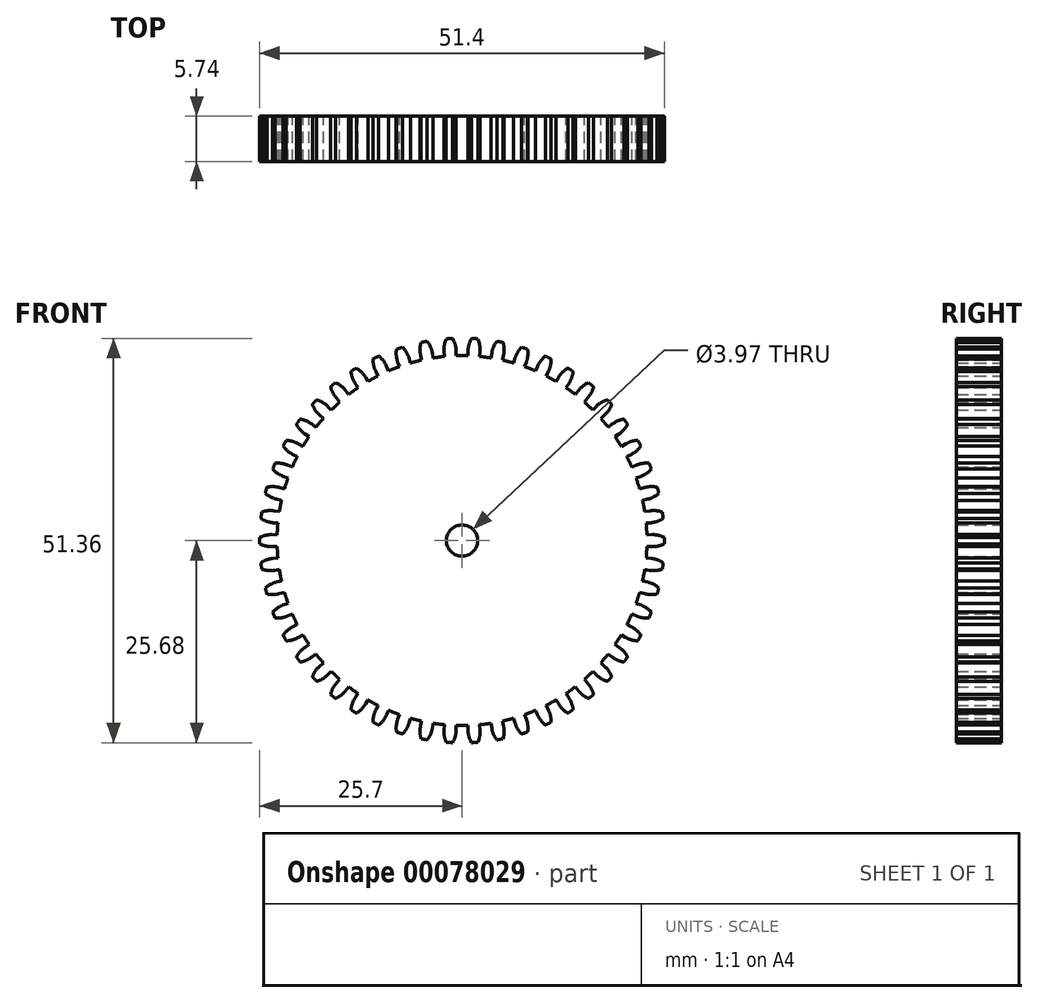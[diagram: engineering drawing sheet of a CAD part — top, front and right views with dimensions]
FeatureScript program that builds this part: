
annotation { "Feature Type Name" : "Feature", "Feature Type Description" : "" }
export const myFeature = defineFeature(function(context is Context, id is Id, definition is map)
    precondition{}
    {
        {
            var Q0;
            Q0=qCreatedBy(makeId("Front.planeOp"),FACE);
            var sketch = newSketch(context, id + "F0", { "sketchPlane" : qUnion([Q0])});
            skCircle(sketch, "E0", {"center": v(0, 0) * mm, "radius": 25.7 * mm, "construction": true});
            skCircle(sketch, "E1", {"center": v(0, 0) * mm, "radius": 24.13 * mm, "construction": true});
            skCircle(sketch, "E2", {"center": v(0, 0) * mm, "radius": 23.5 * mm, "construction": true});
            skLineSegment(sketch, "E3", {"start": v(0, 0) * mm, "end": v(23.45, 1.48) * mm, "construction": true});
            skLineSegment(sketch, "E4", {"start": v(0, 0) * mm, "end": v(6.61, 0) * mm, "construction": true});
            skLineSegment(sketch, "E5", {"start": v(0, 0) * mm, "end": v(6.9, 0.22) * mm, "construction": true});
            skLineSegment(sketch, "E6", {"start": v(0, 0) * mm, "end": v(7.15, 0.11) * mm, "construction": true});
            skArc(sketch, "E7", {"start": v(25.7, 0.4) * mm, "mid": v(25.7, 0.2) * mm, "end": v(25.7, 0) * mm});
            skArc(sketch, "E8", {"start": v(23.45, 1.48) * mm, "mid": v(23.47, 1.1) * mm, "end": v(23.48, 0.74) * mm});
            skLineSegment(sketch, "E9", {"start": v(23.48, 0.74) * mm, "end": v(24.12, 0.76) * mm});
            skArc(sketch, "E10", {"start": v(24.12, 0.76) * mm, "mid": v(24.93, 0.68) * mm, "end": v(25.7, 0.4) * mm});
            skLineSegment(sketch, "E11", {"start": v(0, 0) * mm, "end": v(23.45, 1.48) * mm});
            skLineSegment(sketch, "E12", {"start": v(0, 0) * mm, "end": v(25.7, 0) * mm});
            skArc(sketch, "E13.MirrorCS", {"start": v(23.45, -1.48) * mm, "mid": v(23.47, -1.1) * mm, "end": v(23.48, -0.74) * mm});
            skLineSegment(sketch, "E14.MirrorCS", {"start": v(23.48, -0.74) * mm, "end": v(24.12, -0.76) * mm});
            skArc(sketch, "E15.MirrorCS", {"start": v(24.12, -0.76) * mm, "mid": v(24.93, -0.68) * mm, "end": v(25.7, -0.4) * mm});
            skArc(sketch, "E16.MirrorCS", {"start": v(25.7, -0.4) * mm, "mid": v(25.7, -0.2) * mm, "end": v(25.7, 0) * mm});
            skArc(sketch, "E17.1.0", {"start": v(23.08, 4.4) * mm, "mid": v(23.15, 4.04) * mm, "end": v(23.2, 3.68) * mm});
            skLineSegment(sketch, "E17.1.1", {"start": v(23.2, 3.68) * mm, "end": v(23.83, 3.77) * mm});
            skArc(sketch, "E17.1.2", {"start": v(23.83, 3.77) * mm, "mid": v(24.65, 3.8) * mm, "end": v(25.45, 3.62) * mm});
            skArc(sketch, "E17.1.3", {"start": v(25.45, 3.62) * mm, "mid": v(25.48, 3.42) * mm, "end": v(25.5, 3.22) * mm});
            skArc(sketch, "E17.1.4", {"start": v(25.55, 2.82) * mm, "mid": v(25.53, 3.02) * mm, "end": v(25.5, 3.22) * mm});
            skArc(sketch, "E17.1.5", {"start": v(24.02, 2.27) * mm, "mid": v(24.82, 2.45) * mm, "end": v(25.55, 2.82) * mm});
            skLineSegment(sketch, "E17.1.6", {"start": v(23.4, 2.21) * mm, "end": v(24.02, 2.27) * mm});
            skArc(sketch, "E17.1.7", {"start": v(23.45, 1.48) * mm, "mid": v(23.42, 1.84) * mm, "end": v(23.4, 2.21) * mm});
            skArc(sketch, "E17.2.0", {"start": v(22.35, 7.26) * mm, "mid": v(22.46, 6.9) * mm, "end": v(22.56, 6.55) * mm});
            skLineSegment(sketch, "E17.2.1", {"start": v(22.56, 6.55) * mm, "end": v(23.17, 6.73) * mm});
            skArc(sketch, "E17.2.2", {"start": v(23.17, 6.73) * mm, "mid": v(23.98, 6.86) * mm, "end": v(24.8, 6.78) * mm});
            skArc(sketch, "E17.2.3", {"start": v(24.8, 6.78) * mm, "mid": v(24.85, 6.59) * mm, "end": v(24.9, 6.4) * mm});
            skArc(sketch, "E17.2.4", {"start": v(25, 6) * mm, "mid": v(24.95, 6.2) * mm, "end": v(24.9, 6.4) * mm});
            skArc(sketch, "E17.2.5", {"start": v(23.55, 5.26) * mm, "mid": v(24.32, 5.54) * mm, "end": v(25, 6) * mm});
            skLineSegment(sketch, "E17.2.6", {"start": v(22.93, 5.13) * mm, "end": v(23.55, 5.26) * mm});
            skArc(sketch, "E17.2.7", {"start": v(23.08, 4.4) * mm, "mid": v(23, 4.76) * mm, "end": v(22.93, 5.13) * mm});
            skArc(sketch, "E17.3.0", {"start": v(21.26, 10) * mm, "mid": v(21.41, 9.67) * mm, "end": v(21.56, 9.33) * mm});
            skLineSegment(sketch, "E17.3.1", {"start": v(21.56, 9.33) * mm, "end": v(22.15, 9.58) * mm});
            skArc(sketch, "E17.3.2", {"start": v(22.15, 9.58) * mm, "mid": v(22.93, 9.81) * mm, "end": v(23.75, 9.84) * mm});
            skArc(sketch, "E17.3.3", {"start": v(23.75, 9.84) * mm, "mid": v(23.82, 9.65) * mm, "end": v(23.9, 9.46) * mm});
            skArc(sketch, "E17.3.4", {"start": v(24.05, 9.09) * mm, "mid": v(23.97, 9.27) * mm, "end": v(23.9, 9.46) * mm});
            skArc(sketch, "E17.3.5", {"start": v(22.7, 8.17) * mm, "mid": v(23.43, 8.55) * mm, "end": v(24.05, 9.09) * mm});
            skLineSegment(sketch, "E17.3.6", {"start": v(22.1, 7.96) * mm, "end": v(22.7, 8.17) * mm});
            skArc(sketch, "E17.3.7", {"start": v(22.35, 7.26) * mm, "mid": v(22.23, 7.61) * mm, "end": v(22.1, 7.96) * mm});
            skArc(sketch, "E17.4.0", {"start": v(19.84, 12.59) * mm, "mid": v(20.03, 12.28) * mm, "end": v(20.22, 11.96) * mm});
            skLineSegment(sketch, "E17.4.1", {"start": v(20.22, 11.96) * mm, "end": v(20.77, 12.28) * mm});
            skArc(sketch, "E17.4.2", {"start": v(20.77, 12.28) * mm, "mid": v(21.52, 12.6) * mm, "end": v(22.33, 12.74) * mm});
            skArc(sketch, "E17.4.3", {"start": v(22.33, 12.74) * mm, "mid": v(22.43, 12.56) * mm, "end": v(22.53, 12.38) * mm});
            skArc(sketch, "E17.4.4", {"start": v(22.72, 12.03) * mm, "mid": v(22.62, 12.2) * mm, "end": v(22.53, 12.38) * mm});
            skArc(sketch, "E17.4.5", {"start": v(21.5, 10.95) * mm, "mid": v(22.18, 11.41) * mm, "end": v(22.72, 12.03) * mm});
            skLineSegment(sketch, "E17.4.6", {"start": v(20.93, 10.67) * mm, "end": v(21.5, 10.95) * mm});
            skArc(sketch, "E17.4.7", {"start": v(21.26, 10) * mm, "mid": v(21.1, 10.34) * mm, "end": v(20.93, 10.67) * mm});
            skArc(sketch, "E17.5.0", {"start": v(18.1, 14.98) * mm, "mid": v(18.34, 14.7) * mm, "end": v(18.56, 14.4) * mm});
            skLineSegment(sketch, "E17.5.1", {"start": v(18.56, 14.4) * mm, "end": v(19.07, 14.79) * mm});
            skArc(sketch, "E17.5.2", {"start": v(19.07, 14.79) * mm, "mid": v(19.77, 15.2) * mm, "end": v(20.56, 15.43) * mm});
            skArc(sketch, "E17.5.3", {"start": v(20.56, 15.43) * mm, "mid": v(20.68, 15.27) * mm, "end": v(20.8, 15.1) * mm});
            skArc(sketch, "E17.5.4", {"start": v(21.03, 14.78) * mm, "mid": v(20.91, 14.95) * mm, "end": v(20.8, 15.1) * mm});
            skArc(sketch, "E17.5.5", {"start": v(19.96, 13.56) * mm, "mid": v(20.57, 14.1) * mm, "end": v(21.03, 14.78) * mm});
            skLineSegment(sketch, "E17.5.6", {"start": v(19.43, 13.2) * mm, "end": v(19.96, 13.56) * mm});
            skArc(sketch, "E17.5.7", {"start": v(19.84, 12.59) * mm, "mid": v(19.64, 12.9) * mm, "end": v(19.43, 13.2) * mm});
            skArc(sketch, "E17.6.0", {"start": v(16.08, 17.13) * mm, "mid": v(16.35, 16.87) * mm, "end": v(16.61, 16.61) * mm});
            skLineSegment(sketch, "E17.6.1", {"start": v(16.61, 16.61) * mm, "end": v(17.06, 17.06) * mm});
            skArc(sketch, "E17.6.2", {"start": v(17.06, 17.06) * mm, "mid": v(17.7, 17.56) * mm, "end": v(18.46, 17.89) * mm});
            skArc(sketch, "E17.6.3", {"start": v(18.46, 17.89) * mm, "mid": v(18.6, 17.74) * mm, "end": v(18.74, 17.6) * mm});
            skArc(sketch, "E17.6.4", {"start": v(19.01, 17.3) * mm, "mid": v(18.88, 17.45) * mm, "end": v(18.74, 17.6) * mm});
            skArc(sketch, "E17.6.5", {"start": v(18.1, 15.96) * mm, "mid": v(18.64, 16.57) * mm, "end": v(19.01, 17.3) * mm});
            skLineSegment(sketch, "E17.6.6", {"start": v(17.62, 15.54) * mm, "end": v(18.1, 15.96) * mm});
            skArc(sketch, "E17.6.7", {"start": v(18.1, 14.98) * mm, "mid": v(17.87, 15.26) * mm, "end": v(17.62, 15.54) * mm});
            skArc(sketch, "E17.7.0", {"start": v(13.81, 19) * mm, "mid": v(14.1, 18.79) * mm, "end": v(14.4, 18.56) * mm});
            skLineSegment(sketch, "E17.7.1", {"start": v(14.4, 18.56) * mm, "end": v(14.79, 19.07) * mm});
            skArc(sketch, "E17.7.2", {"start": v(14.79, 19.07) * mm, "mid": v(15.37, 19.64) * mm, "end": v(16.07, 20.06) * mm});
            skArc(sketch, "E17.7.3", {"start": v(16.07, 20.06) * mm, "mid": v(16.23, 19.93) * mm, "end": v(16.38, 19.8) * mm});
            skArc(sketch, "E17.7.4", {"start": v(16.7, 19.55) * mm, "mid": v(16.54, 19.68) * mm, "end": v(16.38, 19.8) * mm});
            skArc(sketch, "E17.7.5", {"start": v(15.96, 18.1) * mm, "mid": v(16.42, 18.78) * mm, "end": v(16.7, 19.55) * mm});
            skLineSegment(sketch, "E17.7.6", {"start": v(15.54, 17.62) * mm, "end": v(15.96, 18.1) * mm});
            skArc(sketch, "E17.7.7", {"start": v(16.08, 17.13) * mm, "mid": v(15.81, 17.38) * mm, "end": v(15.54, 17.62) * mm});
            skArc(sketch, "E17.8.0", {"start": v(11.32, 20.59) * mm, "mid": v(11.64, 20.4) * mm, "end": v(11.96, 20.22) * mm});
            skLineSegment(sketch, "E17.8.1", {"start": v(11.96, 20.22) * mm, "end": v(12.28, 20.77) * mm});
            skArc(sketch, "E17.8.2", {"start": v(12.28, 20.77) * mm, "mid": v(12.78, 21.42) * mm, "end": v(13.43, 21.92) * mm});
            skArc(sketch, "E17.8.3", {"start": v(13.43, 21.92) * mm, "mid": v(13.6, 21.81) * mm, "end": v(13.77, 21.7) * mm});
            skArc(sketch, "E17.8.4", {"start": v(14.11, 21.48) * mm, "mid": v(13.94, 21.6) * mm, "end": v(13.77, 21.7) * mm});
            skArc(sketch, "E17.8.5", {"start": v(13.56, 19.96) * mm, "mid": v(13.93, 20.69) * mm, "end": v(14.11, 21.48) * mm});
            skLineSegment(sketch, "E17.8.6", {"start": v(13.2, 19.43) * mm, "end": v(13.56, 19.96) * mm});
            skArc(sketch, "E17.8.7", {"start": v(13.81, 19) * mm, "mid": v(13.5, 19.22) * mm, "end": v(13.2, 19.43) * mm});
            skArc(sketch, "E17.9.0", {"start": v(8.65, 21.85) * mm, "mid": v(9, 21.7) * mm, "end": v(9.33, 21.56) * mm});
            skLineSegment(sketch, "E17.9.1", {"start": v(9.33, 21.56) * mm, "end": v(9.58, 22.15) * mm});
            skArc(sketch, "E17.9.2", {"start": v(9.58, 22.15) * mm, "mid": v(10, 22.85) * mm, "end": v(10.58, 23.43) * mm});
            skArc(sketch, "E17.9.3", {"start": v(10.58, 23.43) * mm, "mid": v(10.76, 23.34) * mm, "end": v(10.94, 23.26) * mm});
            skArc(sketch, "E17.9.4", {"start": v(11.3, 23.08) * mm, "mid": v(11.13, 23.17) * mm, "end": v(10.94, 23.26) * mm});
            skArc(sketch, "E17.9.5", {"start": v(10.95, 21.5) * mm, "mid": v(11.23, 22.27) * mm, "end": v(11.3, 23.08) * mm});
            skLineSegment(sketch, "E17.9.6", {"start": v(10.67, 20.93) * mm, "end": v(10.95, 21.5) * mm});
            skArc(sketch, "E17.9.7", {"start": v(11.32, 20.59) * mm, "mid": v(11, 20.76) * mm, "end": v(10.67, 20.93) * mm});
            skCircle(sketch, "E18", {"center": v(0, 0) * mm, "radius": 1.98 * mm});
            skArc(sketch, "E19.1.10.0", {"start": v(5.84, 22.76) * mm, "mid": v(6.2, 22.66) * mm, "end": v(6.55, 22.56) * mm});
            skLineSegment(sketch, "E19.4.10.0", {"start": v(6.55, 22.56) * mm, "end": v(6.73, 23.17) * mm});
            skArc(sketch, "E19.7.10.0", {"start": v(6.73, 23.17) * mm, "mid": v(7.06, 23.92) * mm, "end": v(7.56, 24.57) * mm});
            skArc(sketch, "E19.11.10.0", {"start": v(7.56, 24.57) * mm, "mid": v(7.75, 24.5) * mm, "end": v(7.94, 24.45) * mm});
            skArc(sketch, "E19.15.10.0", {"start": v(8.33, 24.32) * mm, "mid": v(8.13, 24.38) * mm, "end": v(7.94, 24.45) * mm});
            skArc(sketch, "E19.19.10.0", {"start": v(8.17, 22.7) * mm, "mid": v(8.35, 23.5) * mm, "end": v(8.33, 24.32) * mm});
            skLineSegment(sketch, "E19.23.10.0", {"start": v(7.96, 22.1) * mm, "end": v(8.17, 22.7) * mm});
            skArc(sketch, "E19.26.10.0", {"start": v(8.65, 21.85) * mm, "mid": v(8.3, 21.98) * mm, "end": v(7.96, 22.1) * mm});
            skArc(sketch, "E19.1.11.0", {"start": v(2.94, 23.3) * mm, "mid": v(3.31, 23.26) * mm, "end": v(3.68, 23.2) * mm});
            skLineSegment(sketch, "E19.4.11.0", {"start": v(3.68, 23.2) * mm, "end": v(3.77, 23.83) * mm});
            skArc(sketch, "E19.7.11.0", {"start": v(3.77, 23.83) * mm, "mid": v(4, 24.62) * mm, "end": v(4.42, 25.32) * mm});
            skArc(sketch, "E19.11.11.0", {"start": v(4.42, 25.32) * mm, "mid": v(4.62, 25.29) * mm, "end": v(4.82, 25.25) * mm});
            skArc(sketch, "E19.15.11.0", {"start": v(5.21, 25.17) * mm, "mid": v(5.01, 25.21) * mm, "end": v(4.82, 25.25) * mm});
            skArc(sketch, "E19.19.11.0", {"start": v(5.26, 23.55) * mm, "mid": v(5.34, 24.36) * mm, "end": v(5.21, 25.17) * mm});
            skLineSegment(sketch, "E19.23.11.0", {"start": v(5.13, 22.93) * mm, "end": v(5.26, 23.55) * mm});
            skArc(sketch, "E19.26.11.0", {"start": v(5.84, 22.76) * mm, "mid": v(5.48, 22.85) * mm, "end": v(5.13, 22.93) * mm});
            skArc(sketch, "E19.1.12.0", {"start": v(0, 23.5) * mm, "mid": v(0.37, 23.5) * mm, "end": v(0.74, 23.48) * mm});
            skLineSegment(sketch, "E19.4.12.0", {"start": v(0.74, 23.48) * mm, "end": v(0.76, 24.12) * mm});
            skArc(sketch, "E19.7.12.0", {"start": v(0.76, 24.12) * mm, "mid": v(0.89, 24.93) * mm, "end": v(1.21, 25.68) * mm});
            skArc(sketch, "E19.11.12.0", {"start": v(1.21, 25.68) * mm, "mid": v(1.41, 25.67) * mm, "end": v(1.61, 25.65) * mm});
            skArc(sketch, "E19.15.12.0", {"start": v(2.02, 25.63) * mm, "mid": v(1.82, 25.64) * mm, "end": v(1.61, 25.65) * mm});
            skArc(sketch, "E19.19.12.0", {"start": v(2.27, 24.02) * mm, "mid": v(2.25, 24.84) * mm, "end": v(2.02, 25.63) * mm});
            skLineSegment(sketch, "E19.23.12.0", {"start": v(2.21, 23.4) * mm, "end": v(2.27, 24.02) * mm});
            skArc(sketch, "E19.26.12.0", {"start": v(2.94, 23.3) * mm, "mid": v(2.58, 23.35) * mm, "end": v(2.21, 23.4) * mm});
            skArc(sketch, "E19.1.13.0", {"start": v(-2.94, 23.3) * mm, "mid": v(-2.58, 23.35) * mm, "end": v(-2.21, 23.4) * mm});
            skLineSegment(sketch, "E19.4.13.0", {"start": v(-2.21, 23.4) * mm, "end": v(-2.27, 24.02) * mm});
            skArc(sketch, "E19.7.13.0", {"start": v(-2.27, 24.02) * mm, "mid": v(-2.25, 24.84) * mm, "end": v(-2.02, 25.63) * mm});
            skArc(sketch, "E19.11.13.0", {"start": v(-2.02, 25.63) * mm, "mid": v(-1.82, 25.64) * mm, "end": v(-1.61, 25.65) * mm});
            skArc(sketch, "E19.15.13.0", {"start": v(-1.21, 25.68) * mm, "mid": v(-1.41, 25.67) * mm, "end": v(-1.61, 25.65) * mm});
            skArc(sketch, "E19.19.13.0", {"start": v(-0.76, 24.12) * mm, "mid": v(-0.89, 24.93) * mm, "end": v(-1.21, 25.68) * mm});
            skLineSegment(sketch, "E19.23.13.0", {"start": v(-0.74, 23.48) * mm, "end": v(-0.76, 24.12) * mm});
            skArc(sketch, "E19.26.13.0", {"start": v(0, 23.5) * mm, "mid": v(-0.37, 23.5) * mm, "end": v(-0.74, 23.48) * mm});
            skArc(sketch, "E19.1.14.0", {"start": v(-5.84, 22.76) * mm, "mid": v(-5.48, 22.85) * mm, "end": v(-5.13, 22.93) * mm});
            skLineSegment(sketch, "E19.4.14.0", {"start": v(-5.13, 22.93) * mm, "end": v(-5.26, 23.55) * mm});
            skArc(sketch, "E19.7.14.0", {"start": v(-5.26, 23.55) * mm, "mid": v(-5.34, 24.36) * mm, "end": v(-5.21, 25.17) * mm});
            skArc(sketch, "E19.11.14.0", {"start": v(-5.21, 25.17) * mm, "mid": v(-5.01, 25.21) * mm, "end": v(-4.82, 25.25) * mm});
            skArc(sketch, "E19.15.14.0", {"start": v(-4.42, 25.32) * mm, "mid": v(-4.62, 25.29) * mm, "end": v(-4.82, 25.25) * mm});
            skArc(sketch, "E19.19.14.0", {"start": v(-3.77, 23.83) * mm, "mid": v(-4, 24.62) * mm, "end": v(-4.42, 25.32) * mm});
            skLineSegment(sketch, "E19.23.14.0", {"start": v(-3.68, 23.2) * mm, "end": v(-3.77, 23.83) * mm});
            skArc(sketch, "E19.26.14.0", {"start": v(-2.94, 23.3) * mm, "mid": v(-3.31, 23.26) * mm, "end": v(-3.68, 23.2) * mm});
            skArc(sketch, "E19.1.15.0", {"start": v(-8.65, 21.85) * mm, "mid": v(-8.3, 21.98) * mm, "end": v(-7.96, 22.1) * mm});
            skLineSegment(sketch, "E19.4.15.0", {"start": v(-7.96, 22.1) * mm, "end": v(-8.17, 22.7) * mm});
            skArc(sketch, "E19.7.15.0", {"start": v(-8.17, 22.7) * mm, "mid": v(-8.35, 23.5) * mm, "end": v(-8.33, 24.32) * mm});
            skArc(sketch, "E19.11.15.0", {"start": v(-8.33, 24.32) * mm, "mid": v(-8.13, 24.38) * mm, "end": v(-7.94, 24.45) * mm});
            skArc(sketch, "E19.15.15.0", {"start": v(-7.56, 24.57) * mm, "mid": v(-7.75, 24.5) * mm, "end": v(-7.94, 24.45) * mm});
            skArc(sketch, "E19.19.15.0", {"start": v(-6.73, 23.17) * mm, "mid": v(-7.06, 23.92) * mm, "end": v(-7.56, 24.57) * mm});
            skLineSegment(sketch, "E19.23.15.0", {"start": v(-6.55, 22.56) * mm, "end": v(-6.73, 23.17) * mm});
            skArc(sketch, "E19.26.15.0", {"start": v(-5.84, 22.76) * mm, "mid": v(-6.2, 22.66) * mm, "end": v(-6.55, 22.56) * mm});
            skArc(sketch, "E19.1.16.0", {"start": v(-11.32, 20.59) * mm, "mid": v(-11, 20.76) * mm, "end": v(-10.67, 20.93) * mm});
            skLineSegment(sketch, "E19.4.16.0", {"start": v(-10.67, 20.93) * mm, "end": v(-10.95, 21.5) * mm});
            skArc(sketch, "E19.7.16.0", {"start": v(-10.95, 21.5) * mm, "mid": v(-11.23, 22.27) * mm, "end": v(-11.3, 23.08) * mm});
            skArc(sketch, "E19.11.16.0", {"start": v(-11.3, 23.08) * mm, "mid": v(-11.13, 23.17) * mm, "end": v(-10.94, 23.26) * mm});
            skArc(sketch, "E19.15.16.0", {"start": v(-10.58, 23.43) * mm, "mid": v(-10.76, 23.34) * mm, "end": v(-10.94, 23.26) * mm});
            skArc(sketch, "E19.19.16.0", {"start": v(-9.58, 22.15) * mm, "mid": v(-10, 22.85) * mm, "end": v(-10.58, 23.43) * mm});
            skLineSegment(sketch, "E19.23.16.0", {"start": v(-9.33, 21.56) * mm, "end": v(-9.58, 22.15) * mm});
            skArc(sketch, "E19.26.16.0", {"start": v(-8.65, 21.85) * mm, "mid": v(-9, 21.7) * mm, "end": v(-9.33, 21.56) * mm});
            skArc(sketch, "E19.1.17.0", {"start": v(-13.81, 19) * mm, "mid": v(-13.5, 19.22) * mm, "end": v(-13.2, 19.43) * mm});
            skLineSegment(sketch, "E19.4.17.0", {"start": v(-13.2, 19.43) * mm, "end": v(-13.56, 19.96) * mm});
            skArc(sketch, "E19.7.17.0", {"start": v(-13.56, 19.96) * mm, "mid": v(-13.93, 20.69) * mm, "end": v(-14.11, 21.48) * mm});
            skArc(sketch, "E19.11.17.0", {"start": v(-14.11, 21.48) * mm, "mid": v(-13.94, 21.6) * mm, "end": v(-13.77, 21.7) * mm});
            skArc(sketch, "E19.15.17.0", {"start": v(-13.43, 21.92) * mm, "mid": v(-13.6, 21.81) * mm, "end": v(-13.77, 21.7) * mm});
            skArc(sketch, "E19.19.17.0", {"start": v(-12.28, 20.77) * mm, "mid": v(-12.78, 21.42) * mm, "end": v(-13.43, 21.92) * mm});
            skLineSegment(sketch, "E19.23.17.0", {"start": v(-11.96, 20.22) * mm, "end": v(-12.28, 20.77) * mm});
            skArc(sketch, "E19.26.17.0", {"start": v(-11.32, 20.59) * mm, "mid": v(-11.64, 20.4) * mm, "end": v(-11.96, 20.22) * mm});
            skArc(sketch, "E19.1.18.0", {"start": v(-16.08, 17.13) * mm, "mid": v(-15.81, 17.38) * mm, "end": v(-15.54, 17.62) * mm});
            skLineSegment(sketch, "E19.4.18.0", {"start": v(-15.54, 17.62) * mm, "end": v(-15.96, 18.1) * mm});
            skArc(sketch, "E19.7.18.0", {"start": v(-15.96, 18.1) * mm, "mid": v(-16.42, 18.78) * mm, "end": v(-16.7, 19.55) * mm});
            skArc(sketch, "E19.11.18.0", {"start": v(-16.7, 19.55) * mm, "mid": v(-16.54, 19.68) * mm, "end": v(-16.38, 19.8) * mm});
            skArc(sketch, "E19.15.18.0", {"start": v(-16.07, 20.06) * mm, "mid": v(-16.23, 19.93) * mm, "end": v(-16.38, 19.8) * mm});
            skArc(sketch, "E19.19.18.0", {"start": v(-14.79, 19.07) * mm, "mid": v(-15.37, 19.64) * mm, "end": v(-16.07, 20.06) * mm});
            skLineSegment(sketch, "E19.23.18.0", {"start": v(-14.4, 18.56) * mm, "end": v(-14.79, 19.07) * mm});
            skArc(sketch, "E19.26.18.0", {"start": v(-13.81, 19) * mm, "mid": v(-14.1, 18.79) * mm, "end": v(-14.4, 18.56) * mm});
            skArc(sketch, "E19.1.19.0", {"start": v(-18.1, 14.98) * mm, "mid": v(-17.87, 15.26) * mm, "end": v(-17.62, 15.54) * mm});
            skLineSegment(sketch, "E19.4.19.0", {"start": v(-17.62, 15.54) * mm, "end": v(-18.1, 15.96) * mm});
            skArc(sketch, "E19.7.19.0", {"start": v(-18.1, 15.96) * mm, "mid": v(-18.64, 16.57) * mm, "end": v(-19.01, 17.3) * mm});
            skArc(sketch, "E19.11.19.0", {"start": v(-19.01, 17.3) * mm, "mid": v(-18.88, 17.45) * mm, "end": v(-18.74, 17.6) * mm});
            skArc(sketch, "E19.15.19.0", {"start": v(-18.46, 17.89) * mm, "mid": v(-18.6, 17.74) * mm, "end": v(-18.74, 17.6) * mm});
            skArc(sketch, "E19.19.19.0", {"start": v(-17.06, 17.06) * mm, "mid": v(-17.7, 17.56) * mm, "end": v(-18.46, 17.89) * mm});
            skLineSegment(sketch, "E19.23.19.0", {"start": v(-16.61, 16.61) * mm, "end": v(-17.06, 17.06) * mm});
            skArc(sketch, "E19.26.19.0", {"start": v(-16.08, 17.13) * mm, "mid": v(-16.35, 16.87) * mm, "end": v(-16.61, 16.61) * mm});
            skArc(sketch, "E19.1.20.0", {"start": v(-19.84, 12.59) * mm, "mid": v(-19.64, 12.9) * mm, "end": v(-19.43, 13.2) * mm});
            skLineSegment(sketch, "E19.4.20.0", {"start": v(-19.43, 13.2) * mm, "end": v(-19.96, 13.56) * mm});
            skArc(sketch, "E19.7.20.0", {"start": v(-19.96, 13.56) * mm, "mid": v(-20.57, 14.1) * mm, "end": v(-21.03, 14.78) * mm});
            skArc(sketch, "E19.11.20.0", {"start": v(-21.03, 14.78) * mm, "mid": v(-20.91, 14.95) * mm, "end": v(-20.8, 15.1) * mm});
            skArc(sketch, "E19.15.20.0", {"start": v(-20.56, 15.43) * mm, "mid": v(-20.68, 15.27) * mm, "end": v(-20.8, 15.1) * mm});
            skArc(sketch, "E19.19.20.0", {"start": v(-19.07, 14.79) * mm, "mid": v(-19.77, 15.2) * mm, "end": v(-20.56, 15.43) * mm});
            skLineSegment(sketch, "E19.23.20.0", {"start": v(-18.56, 14.4) * mm, "end": v(-19.07, 14.79) * mm});
            skArc(sketch, "E19.26.20.0", {"start": v(-18.1, 14.98) * mm, "mid": v(-18.34, 14.7) * mm, "end": v(-18.56, 14.4) * mm});
            skArc(sketch, "E19.1.21.0", {"start": v(-21.26, 10) * mm, "mid": v(-21.1, 10.34) * mm, "end": v(-20.93, 10.67) * mm});
            skLineSegment(sketch, "E19.4.21.0", {"start": v(-20.93, 10.67) * mm, "end": v(-21.5, 10.95) * mm});
            skArc(sketch, "E19.7.21.0", {"start": v(-21.5, 10.95) * mm, "mid": v(-22.18, 11.41) * mm, "end": v(-22.72, 12.03) * mm});
            skArc(sketch, "E19.11.21.0", {"start": v(-22.72, 12.03) * mm, "mid": v(-22.62, 12.2) * mm, "end": v(-22.53, 12.38) * mm});
            skArc(sketch, "E19.15.21.0", {"start": v(-22.33, 12.74) * mm, "mid": v(-22.43, 12.56) * mm, "end": v(-22.53, 12.38) * mm});
            skArc(sketch, "E19.19.21.0", {"start": v(-20.77, 12.28) * mm, "mid": v(-21.52, 12.6) * mm, "end": v(-22.33, 12.74) * mm});
            skLineSegment(sketch, "E19.23.21.0", {"start": v(-20.22, 11.96) * mm, "end": v(-20.77, 12.28) * mm});
            skArc(sketch, "E19.26.21.0", {"start": v(-19.84, 12.59) * mm, "mid": v(-20.03, 12.28) * mm, "end": v(-20.22, 11.96) * mm});
            skArc(sketch, "E19.1.22.0", {"start": v(-22.35, 7.26) * mm, "mid": v(-22.23, 7.61) * mm, "end": v(-22.1, 7.96) * mm});
            skLineSegment(sketch, "E19.4.22.0", {"start": v(-22.1, 7.96) * mm, "end": v(-22.7, 8.17) * mm});
            skArc(sketch, "E19.7.22.0", {"start": v(-22.7, 8.17) * mm, "mid": v(-23.43, 8.55) * mm, "end": v(-24.05, 9.09) * mm});
            skArc(sketch, "E19.11.22.0", {"start": v(-24.05, 9.09) * mm, "mid": v(-23.97, 9.27) * mm, "end": v(-23.9, 9.46) * mm});
            skArc(sketch, "E19.15.22.0", {"start": v(-23.75, 9.84) * mm, "mid": v(-23.82, 9.65) * mm, "end": v(-23.9, 9.46) * mm});
            skArc(sketch, "E19.19.22.0", {"start": v(-22.15, 9.58) * mm, "mid": v(-22.93, 9.81) * mm, "end": v(-23.75, 9.84) * mm});
            skLineSegment(sketch, "E19.23.22.0", {"start": v(-21.56, 9.33) * mm, "end": v(-22.15, 9.58) * mm});
            skArc(sketch, "E19.26.22.0", {"start": v(-21.26, 10) * mm, "mid": v(-21.41, 9.67) * mm, "end": v(-21.56, 9.33) * mm});
            skArc(sketch, "E19.1.23.0", {"start": v(-23.08, 4.4) * mm, "mid": v(-23, 4.76) * mm, "end": v(-22.93, 5.13) * mm});
            skLineSegment(sketch, "E19.4.23.0", {"start": v(-22.93, 5.13) * mm, "end": v(-23.55, 5.26) * mm});
            skArc(sketch, "E19.7.23.0", {"start": v(-23.55, 5.26) * mm, "mid": v(-24.32, 5.54) * mm, "end": v(-25, 6) * mm});
            skArc(sketch, "E19.11.23.0", {"start": v(-25, 6) * mm, "mid": v(-24.95, 6.2) * mm, "end": v(-24.9, 6.4) * mm});
            skArc(sketch, "E19.15.23.0", {"start": v(-24.8, 6.78) * mm, "mid": v(-24.85, 6.59) * mm, "end": v(-24.9, 6.4) * mm});
            skArc(sketch, "E19.19.23.0", {"start": v(-23.17, 6.73) * mm, "mid": v(-23.98, 6.86) * mm, "end": v(-24.8, 6.78) * mm});
            skLineSegment(sketch, "E19.23.23.0", {"start": v(-22.56, 6.55) * mm, "end": v(-23.17, 6.73) * mm});
            skArc(sketch, "E19.26.23.0", {"start": v(-22.35, 7.26) * mm, "mid": v(-22.46, 6.9) * mm, "end": v(-22.56, 6.55) * mm});
            skArc(sketch, "E19.1.24.0", {"start": v(-23.45, 1.48) * mm, "mid": v(-23.42, 1.84) * mm, "end": v(-23.4, 2.21) * mm});
            skLineSegment(sketch, "E19.4.24.0", {"start": v(-23.4, 2.21) * mm, "end": v(-24.02, 2.27) * mm});
            skArc(sketch, "E19.7.24.0", {"start": v(-24.02, 2.27) * mm, "mid": v(-24.82, 2.45) * mm, "end": v(-25.55, 2.82) * mm});
            skArc(sketch, "E19.11.24.0", {"start": v(-25.55, 2.82) * mm, "mid": v(-25.53, 3.02) * mm, "end": v(-25.5, 3.22) * mm});
            skArc(sketch, "E19.15.24.0", {"start": v(-25.45, 3.62) * mm, "mid": v(-25.48, 3.42) * mm, "end": v(-25.5, 3.22) * mm});
            skArc(sketch, "E19.19.24.0", {"start": v(-23.83, 3.77) * mm, "mid": v(-24.65, 3.8) * mm, "end": v(-25.45, 3.62) * mm});
            skLineSegment(sketch, "E19.23.24.0", {"start": v(-23.2, 3.68) * mm, "end": v(-23.83, 3.77) * mm});
            skArc(sketch, "E19.26.24.0", {"start": v(-23.08, 4.4) * mm, "mid": v(-23.15, 4.04) * mm, "end": v(-23.2, 3.68) * mm});
            skArc(sketch, "E19.1.25.0", {"start": v(-23.45, -1.48) * mm, "mid": v(-23.47, -1.1) * mm, "end": v(-23.48, -0.74) * mm});
            skLineSegment(sketch, "E19.4.25.0", {"start": v(-23.48, -0.74) * mm, "end": v(-24.12, -0.76) * mm});
            skArc(sketch, "E19.7.25.0", {"start": v(-24.12, -0.76) * mm, "mid": v(-24.93, -0.68) * mm, "end": v(-25.7, -0.4) * mm});
            skArc(sketch, "E19.11.25.0", {"start": v(-25.7, -0.4) * mm, "mid": v(-25.7, -0.2) * mm, "end": v(-25.7, 0) * mm});
            skArc(sketch, "E19.15.25.0", {"start": v(-25.7, 0.4) * mm, "mid": v(-25.7, 0.2) * mm, "end": v(-25.7, 0) * mm});
            skArc(sketch, "E19.19.25.0", {"start": v(-24.12, 0.76) * mm, "mid": v(-24.93, 0.68) * mm, "end": v(-25.7, 0.4) * mm});
            skLineSegment(sketch, "E19.23.25.0", {"start": v(-23.48, 0.74) * mm, "end": v(-24.12, 0.76) * mm});
            skArc(sketch, "E19.26.25.0", {"start": v(-23.45, 1.48) * mm, "mid": v(-23.47, 1.1) * mm, "end": v(-23.48, 0.74) * mm});
            skArc(sketch, "E19.1.26.0", {"start": v(-23.08, -4.4) * mm, "mid": v(-23.15, -4.04) * mm, "end": v(-23.2, -3.68) * mm});
            skLineSegment(sketch, "E19.4.26.0", {"start": v(-23.2, -3.68) * mm, "end": v(-23.83, -3.77) * mm});
            skArc(sketch, "E19.7.26.0", {"start": v(-23.83, -3.77) * mm, "mid": v(-24.65, -3.8) * mm, "end": v(-25.45, -3.62) * mm});
            skArc(sketch, "E19.11.26.0", {"start": v(-25.45, -3.62) * mm, "mid": v(-25.48, -3.42) * mm, "end": v(-25.5, -3.22) * mm});
            skArc(sketch, "E19.15.26.0", {"start": v(-25.55, -2.82) * mm, "mid": v(-25.53, -3.02) * mm, "end": v(-25.5, -3.22) * mm});
            skArc(sketch, "E19.19.26.0", {"start": v(-24.02, -2.27) * mm, "mid": v(-24.82, -2.45) * mm, "end": v(-25.55, -2.82) * mm});
            skLineSegment(sketch, "E19.23.26.0", {"start": v(-23.4, -2.21) * mm, "end": v(-24.02, -2.27) * mm});
            skArc(sketch, "E19.26.26.0", {"start": v(-23.45, -1.48) * mm, "mid": v(-23.42, -1.84) * mm, "end": v(-23.4, -2.21) * mm});
            skArc(sketch, "E19.1.27.0", {"start": v(-22.35, -7.26) * mm, "mid": v(-22.46, -6.9) * mm, "end": v(-22.56, -6.55) * mm});
            skLineSegment(sketch, "E19.4.27.0", {"start": v(-22.56, -6.55) * mm, "end": v(-23.17, -6.73) * mm});
            skArc(sketch, "E19.7.27.0", {"start": v(-23.17, -6.73) * mm, "mid": v(-23.98, -6.86) * mm, "end": v(-24.8, -6.78) * mm});
            skArc(sketch, "E19.11.27.0", {"start": v(-24.8, -6.78) * mm, "mid": v(-24.85, -6.59) * mm, "end": v(-24.9, -6.4) * mm});
            skArc(sketch, "E19.15.27.0", {"start": v(-25, -6) * mm, "mid": v(-24.95, -6.2) * mm, "end": v(-24.9, -6.4) * mm});
            skArc(sketch, "E19.19.27.0", {"start": v(-23.55, -5.26) * mm, "mid": v(-24.32, -5.54) * mm, "end": v(-25, -6) * mm});
            skLineSegment(sketch, "E19.23.27.0", {"start": v(-22.93, -5.13) * mm, "end": v(-23.55, -5.26) * mm});
            skArc(sketch, "E19.26.27.0", {"start": v(-23.08, -4.4) * mm, "mid": v(-23, -4.76) * mm, "end": v(-22.93, -5.13) * mm});
            skArc(sketch, "E19.1.28.0", {"start": v(-21.26, -10) * mm, "mid": v(-21.41, -9.67) * mm, "end": v(-21.56, -9.33) * mm});
            skLineSegment(sketch, "E19.4.28.0", {"start": v(-21.56, -9.33) * mm, "end": v(-22.15, -9.58) * mm});
            skArc(sketch, "E19.7.28.0", {"start": v(-22.15, -9.58) * mm, "mid": v(-22.93, -9.81) * mm, "end": v(-23.75, -9.84) * mm});
            skArc(sketch, "E19.11.28.0", {"start": v(-23.75, -9.84) * mm, "mid": v(-23.82, -9.65) * mm, "end": v(-23.9, -9.46) * mm});
            skArc(sketch, "E19.15.28.0", {"start": v(-24.05, -9.09) * mm, "mid": v(-23.97, -9.27) * mm, "end": v(-23.9, -9.46) * mm});
            skArc(sketch, "E19.19.28.0", {"start": v(-22.7, -8.17) * mm, "mid": v(-23.43, -8.55) * mm, "end": v(-24.05, -9.09) * mm});
            skLineSegment(sketch, "E19.23.28.0", {"start": v(-22.1, -7.96) * mm, "end": v(-22.7, -8.17) * mm});
            skArc(sketch, "E19.26.28.0", {"start": v(-22.35, -7.26) * mm, "mid": v(-22.23, -7.61) * mm, "end": v(-22.1, -7.96) * mm});
            skArc(sketch, "E19.1.29.0", {"start": v(-19.84, -12.59) * mm, "mid": v(-20.03, -12.28) * mm, "end": v(-20.22, -11.96) * mm});
            skLineSegment(sketch, "E19.4.29.0", {"start": v(-20.22, -11.96) * mm, "end": v(-20.77, -12.28) * mm});
            skArc(sketch, "E19.7.29.0", {"start": v(-20.77, -12.28) * mm, "mid": v(-21.52, -12.6) * mm, "end": v(-22.33, -12.74) * mm});
            skArc(sketch, "E19.11.29.0", {"start": v(-22.33, -12.74) * mm, "mid": v(-22.43, -12.56) * mm, "end": v(-22.53, -12.38) * mm});
            skArc(sketch, "E19.15.29.0", {"start": v(-22.72, -12.03) * mm, "mid": v(-22.62, -12.2) * mm, "end": v(-22.53, -12.38) * mm});
            skArc(sketch, "E19.19.29.0", {"start": v(-21.5, -10.95) * mm, "mid": v(-22.18, -11.41) * mm, "end": v(-22.72, -12.03) * mm});
            skLineSegment(sketch, "E19.23.29.0", {"start": v(-20.93, -10.67) * mm, "end": v(-21.5, -10.95) * mm});
            skArc(sketch, "E19.26.29.0", {"start": v(-21.26, -10) * mm, "mid": v(-21.1, -10.34) * mm, "end": v(-20.93, -10.67) * mm});
            skArc(sketch, "E19.1.30.0", {"start": v(-18.1, -14.98) * mm, "mid": v(-18.34, -14.7) * mm, "end": v(-18.56, -14.4) * mm});
            skLineSegment(sketch, "E19.4.30.0", {"start": v(-18.56, -14.4) * mm, "end": v(-19.07, -14.79) * mm});
            skArc(sketch, "E19.7.30.0", {"start": v(-19.07, -14.79) * mm, "mid": v(-19.77, -15.2) * mm, "end": v(-20.56, -15.43) * mm});
            skArc(sketch, "E19.11.30.0", {"start": v(-20.56, -15.43) * mm, "mid": v(-20.68, -15.27) * mm, "end": v(-20.8, -15.1) * mm});
            skArc(sketch, "E19.15.30.0", {"start": v(-21.03, -14.78) * mm, "mid": v(-20.91, -14.95) * mm, "end": v(-20.8, -15.1) * mm});
            skArc(sketch, "E19.19.30.0", {"start": v(-19.96, -13.56) * mm, "mid": v(-20.57, -14.1) * mm, "end": v(-21.03, -14.78) * mm});
            skLineSegment(sketch, "E19.23.30.0", {"start": v(-19.43, -13.2) * mm, "end": v(-19.96, -13.56) * mm});
            skArc(sketch, "E19.26.30.0", {"start": v(-19.84, -12.59) * mm, "mid": v(-19.64, -12.9) * mm, "end": v(-19.43, -13.2) * mm});
            skArc(sketch, "E19.1.31.0", {"start": v(-16.08, -17.13) * mm, "mid": v(-16.35, -16.87) * mm, "end": v(-16.61, -16.61) * mm});
            skLineSegment(sketch, "E19.4.31.0", {"start": v(-16.61, -16.61) * mm, "end": v(-17.06, -17.06) * mm});
            skArc(sketch, "E19.7.31.0", {"start": v(-17.06, -17.06) * mm, "mid": v(-17.7, -17.56) * mm, "end": v(-18.46, -17.89) * mm});
            skArc(sketch, "E19.11.31.0", {"start": v(-18.46, -17.89) * mm, "mid": v(-18.6, -17.74) * mm, "end": v(-18.74, -17.6) * mm});
            skArc(sketch, "E19.15.31.0", {"start": v(-19.01, -17.3) * mm, "mid": v(-18.88, -17.45) * mm, "end": v(-18.74, -17.6) * mm});
            skArc(sketch, "E19.19.31.0", {"start": v(-18.1, -15.96) * mm, "mid": v(-18.64, -16.57) * mm, "end": v(-19.01, -17.3) * mm});
            skLineSegment(sketch, "E19.23.31.0", {"start": v(-17.62, -15.54) * mm, "end": v(-18.1, -15.96) * mm});
            skArc(sketch, "E19.26.31.0", {"start": v(-18.1, -14.98) * mm, "mid": v(-17.87, -15.26) * mm, "end": v(-17.62, -15.54) * mm});
            skArc(sketch, "E19.1.32.0", {"start": v(-13.81, -19) * mm, "mid": v(-14.1, -18.79) * mm, "end": v(-14.4, -18.56) * mm});
            skLineSegment(sketch, "E19.4.32.0", {"start": v(-14.4, -18.56) * mm, "end": v(-14.79, -19.07) * mm});
            skArc(sketch, "E19.7.32.0", {"start": v(-14.79, -19.07) * mm, "mid": v(-15.37, -19.64) * mm, "end": v(-16.07, -20.06) * mm});
            skArc(sketch, "E19.11.32.0", {"start": v(-16.07, -20.06) * mm, "mid": v(-16.23, -19.93) * mm, "end": v(-16.38, -19.8) * mm});
            skArc(sketch, "E19.15.32.0", {"start": v(-16.7, -19.55) * mm, "mid": v(-16.54, -19.68) * mm, "end": v(-16.38, -19.8) * mm});
            skArc(sketch, "E19.19.32.0", {"start": v(-15.96, -18.1) * mm, "mid": v(-16.42, -18.78) * mm, "end": v(-16.7, -19.55) * mm});
            skLineSegment(sketch, "E19.23.32.0", {"start": v(-15.54, -17.62) * mm, "end": v(-15.96, -18.1) * mm});
            skArc(sketch, "E19.26.32.0", {"start": v(-16.08, -17.13) * mm, "mid": v(-15.81, -17.38) * mm, "end": v(-15.54, -17.62) * mm});
            skArc(sketch, "E19.1.33.0", {"start": v(-11.32, -20.59) * mm, "mid": v(-11.64, -20.4) * mm, "end": v(-11.96, -20.22) * mm});
            skLineSegment(sketch, "E19.4.33.0", {"start": v(-11.96, -20.22) * mm, "end": v(-12.28, -20.77) * mm});
            skArc(sketch, "E19.7.33.0", {"start": v(-12.28, -20.77) * mm, "mid": v(-12.78, -21.42) * mm, "end": v(-13.43, -21.92) * mm});
            skArc(sketch, "E19.11.33.0", {"start": v(-13.43, -21.92) * mm, "mid": v(-13.6, -21.81) * mm, "end": v(-13.77, -21.7) * mm});
            skArc(sketch, "E19.15.33.0", {"start": v(-14.11, -21.48) * mm, "mid": v(-13.94, -21.6) * mm, "end": v(-13.77, -21.7) * mm});
            skArc(sketch, "E19.19.33.0", {"start": v(-13.56, -19.96) * mm, "mid": v(-13.93, -20.69) * mm, "end": v(-14.11, -21.48) * mm});
            skLineSegment(sketch, "E19.23.33.0", {"start": v(-13.2, -19.43) * mm, "end": v(-13.56, -19.96) * mm});
            skArc(sketch, "E19.26.33.0", {"start": v(-13.81, -19) * mm, "mid": v(-13.5, -19.22) * mm, "end": v(-13.2, -19.43) * mm});
            skArc(sketch, "E19.1.34.0", {"start": v(-8.65, -21.85) * mm, "mid": v(-9, -21.7) * mm, "end": v(-9.33, -21.56) * mm});
            skLineSegment(sketch, "E19.4.34.0", {"start": v(-9.33, -21.56) * mm, "end": v(-9.58, -22.15) * mm});
            skArc(sketch, "E19.7.34.0", {"start": v(-9.58, -22.15) * mm, "mid": v(-10, -22.85) * mm, "end": v(-10.58, -23.43) * mm});
            skArc(sketch, "E19.11.34.0", {"start": v(-10.58, -23.43) * mm, "mid": v(-10.76, -23.34) * mm, "end": v(-10.94, -23.26) * mm});
            skArc(sketch, "E19.15.34.0", {"start": v(-11.3, -23.08) * mm, "mid": v(-11.13, -23.17) * mm, "end": v(-10.94, -23.26) * mm});
            skArc(sketch, "E19.19.34.0", {"start": v(-10.95, -21.5) * mm, "mid": v(-11.23, -22.27) * mm, "end": v(-11.3, -23.08) * mm});
            skLineSegment(sketch, "E19.23.34.0", {"start": v(-10.67, -20.93) * mm, "end": v(-10.95, -21.5) * mm});
            skArc(sketch, "E19.26.34.0", {"start": v(-11.32, -20.59) * mm, "mid": v(-11, -20.76) * mm, "end": v(-10.67, -20.93) * mm});
            skArc(sketch, "E19.1.35.0", {"start": v(-5.84, -22.76) * mm, "mid": v(-6.2, -22.66) * mm, "end": v(-6.55, -22.56) * mm});
            skLineSegment(sketch, "E19.4.35.0", {"start": v(-6.55, -22.56) * mm, "end": v(-6.73, -23.17) * mm});
            skArc(sketch, "E19.7.35.0", {"start": v(-6.73, -23.17) * mm, "mid": v(-7.06, -23.92) * mm, "end": v(-7.56, -24.57) * mm});
            skArc(sketch, "E19.11.35.0", {"start": v(-7.56, -24.57) * mm, "mid": v(-7.75, -24.5) * mm, "end": v(-7.94, -24.45) * mm});
            skArc(sketch, "E19.15.35.0", {"start": v(-8.33, -24.32) * mm, "mid": v(-8.13, -24.38) * mm, "end": v(-7.94, -24.45) * mm});
            skArc(sketch, "E19.19.35.0", {"start": v(-8.17, -22.7) * mm, "mid": v(-8.35, -23.5) * mm, "end": v(-8.33, -24.32) * mm});
            skLineSegment(sketch, "E19.23.35.0", {"start": v(-7.96, -22.1) * mm, "end": v(-8.17, -22.7) * mm});
            skArc(sketch, "E19.26.35.0", {"start": v(-8.65, -21.85) * mm, "mid": v(-8.3, -21.98) * mm, "end": v(-7.96, -22.1) * mm});
            skArc(sketch, "E19.1.36.0", {"start": v(-2.94, -23.3) * mm, "mid": v(-3.31, -23.26) * mm, "end": v(-3.68, -23.2) * mm});
            skLineSegment(sketch, "E19.4.36.0", {"start": v(-3.68, -23.2) * mm, "end": v(-3.77, -23.83) * mm});
            skArc(sketch, "E19.7.36.0", {"start": v(-3.77, -23.83) * mm, "mid": v(-4, -24.62) * mm, "end": v(-4.42, -25.32) * mm});
            skArc(sketch, "E19.11.36.0", {"start": v(-4.42, -25.32) * mm, "mid": v(-4.62, -25.29) * mm, "end": v(-4.82, -25.25) * mm});
            skArc(sketch, "E19.15.36.0", {"start": v(-5.21, -25.17) * mm, "mid": v(-5.01, -25.21) * mm, "end": v(-4.82, -25.25) * mm});
            skArc(sketch, "E19.19.36.0", {"start": v(-5.26, -23.55) * mm, "mid": v(-5.34, -24.36) * mm, "end": v(-5.21, -25.17) * mm});
            skLineSegment(sketch, "E19.23.36.0", {"start": v(-5.13, -22.93) * mm, "end": v(-5.26, -23.55) * mm});
            skArc(sketch, "E19.26.36.0", {"start": v(-5.84, -22.76) * mm, "mid": v(-5.48, -22.85) * mm, "end": v(-5.13, -22.93) * mm});
            skArc(sketch, "E19.1.37.0", {"start": v(0, -23.5) * mm, "mid": v(-0.37, -23.5) * mm, "end": v(-0.74, -23.48) * mm});
            skLineSegment(sketch, "E19.4.37.0", {"start": v(-0.74, -23.48) * mm, "end": v(-0.76, -24.12) * mm});
            skArc(sketch, "E19.7.37.0", {"start": v(-0.76, -24.12) * mm, "mid": v(-0.89, -24.93) * mm, "end": v(-1.21, -25.68) * mm});
            skArc(sketch, "E19.11.37.0", {"start": v(-1.21, -25.68) * mm, "mid": v(-1.41, -25.67) * mm, "end": v(-1.61, -25.65) * mm});
            skArc(sketch, "E19.15.37.0", {"start": v(-2.02, -25.63) * mm, "mid": v(-1.82, -25.64) * mm, "end": v(-1.61, -25.65) * mm});
            skArc(sketch, "E19.19.37.0", {"start": v(-2.27, -24.02) * mm, "mid": v(-2.25, -24.84) * mm, "end": v(-2.02, -25.63) * mm});
            skLineSegment(sketch, "E19.23.37.0", {"start": v(-2.21, -23.4) * mm, "end": v(-2.27, -24.02) * mm});
            skArc(sketch, "E19.26.37.0", {"start": v(-2.94, -23.3) * mm, "mid": v(-2.58, -23.35) * mm, "end": v(-2.21, -23.4) * mm});
            skArc(sketch, "E19.1.38.0", {"start": v(2.94, -23.3) * mm, "mid": v(2.58, -23.35) * mm, "end": v(2.21, -23.4) * mm});
            skLineSegment(sketch, "E19.4.38.0", {"start": v(2.21, -23.4) * mm, "end": v(2.27, -24.02) * mm});
            skArc(sketch, "E19.7.38.0", {"start": v(2.27, -24.02) * mm, "mid": v(2.25, -24.84) * mm, "end": v(2.02, -25.63) * mm});
            skArc(sketch, "E19.11.38.0", {"start": v(2.02, -25.63) * mm, "mid": v(1.82, -25.64) * mm, "end": v(1.61, -25.65) * mm});
            skArc(sketch, "E19.15.38.0", {"start": v(1.21, -25.68) * mm, "mid": v(1.41, -25.67) * mm, "end": v(1.61, -25.65) * mm});
            skArc(sketch, "E19.19.38.0", {"start": v(0.76, -24.12) * mm, "mid": v(0.89, -24.93) * mm, "end": v(1.21, -25.68) * mm});
            skLineSegment(sketch, "E19.23.38.0", {"start": v(0.74, -23.48) * mm, "end": v(0.76, -24.12) * mm});
            skArc(sketch, "E19.26.38.0", {"start": v(0, -23.5) * mm, "mid": v(0.37, -23.5) * mm, "end": v(0.74, -23.48) * mm});
            skArc(sketch, "E19.1.39.0", {"start": v(5.84, -22.76) * mm, "mid": v(5.48, -22.85) * mm, "end": v(5.13, -22.93) * mm});
            skLineSegment(sketch, "E19.4.39.0", {"start": v(5.13, -22.93) * mm, "end": v(5.26, -23.55) * mm});
            skArc(sketch, "E19.7.39.0", {"start": v(5.26, -23.55) * mm, "mid": v(5.34, -24.36) * mm, "end": v(5.21, -25.17) * mm});
            skArc(sketch, "E19.11.39.0", {"start": v(5.21, -25.17) * mm, "mid": v(5.01, -25.21) * mm, "end": v(4.82, -25.25) * mm});
            skArc(sketch, "E19.15.39.0", {"start": v(4.42, -25.32) * mm, "mid": v(4.62, -25.29) * mm, "end": v(4.82, -25.25) * mm});
            skArc(sketch, "E19.19.39.0", {"start": v(3.77, -23.83) * mm, "mid": v(4, -24.62) * mm, "end": v(4.42, -25.32) * mm});
            skLineSegment(sketch, "E19.23.39.0", {"start": v(3.68, -23.2) * mm, "end": v(3.77, -23.83) * mm});
            skArc(sketch, "E19.26.39.0", {"start": v(2.94, -23.3) * mm, "mid": v(3.31, -23.26) * mm, "end": v(3.68, -23.2) * mm});
            skArc(sketch, "E19.1.40.0", {"start": v(8.65, -21.85) * mm, "mid": v(8.3, -21.98) * mm, "end": v(7.96, -22.1) * mm});
            skLineSegment(sketch, "E19.4.40.0", {"start": v(7.96, -22.1) * mm, "end": v(8.17, -22.7) * mm});
            skArc(sketch, "E19.7.40.0", {"start": v(8.17, -22.7) * mm, "mid": v(8.35, -23.5) * mm, "end": v(8.33, -24.32) * mm});
            skArc(sketch, "E19.11.40.0", {"start": v(8.33, -24.32) * mm, "mid": v(8.13, -24.38) * mm, "end": v(7.94, -24.45) * mm});
            skArc(sketch, "E19.15.40.0", {"start": v(7.56, -24.57) * mm, "mid": v(7.75, -24.5) * mm, "end": v(7.94, -24.45) * mm});
            skArc(sketch, "E19.19.40.0", {"start": v(6.73, -23.17) * mm, "mid": v(7.06, -23.92) * mm, "end": v(7.56, -24.57) * mm});
            skLineSegment(sketch, "E19.23.40.0", {"start": v(6.55, -22.56) * mm, "end": v(6.73, -23.17) * mm});
            skArc(sketch, "E19.26.40.0", {"start": v(5.84, -22.76) * mm, "mid": v(6.2, -22.66) * mm, "end": v(6.55, -22.56) * mm});
            skArc(sketch, "E19.1.41.0", {"start": v(11.32, -20.59) * mm, "mid": v(11, -20.76) * mm, "end": v(10.67, -20.93) * mm});
            skLineSegment(sketch, "E19.4.41.0", {"start": v(10.67, -20.93) * mm, "end": v(10.95, -21.5) * mm});
            skArc(sketch, "E19.7.41.0", {"start": v(10.95, -21.5) * mm, "mid": v(11.23, -22.27) * mm, "end": v(11.3, -23.08) * mm});
            skArc(sketch, "E19.11.41.0", {"start": v(11.3, -23.08) * mm, "mid": v(11.13, -23.17) * mm, "end": v(10.94, -23.26) * mm});
            skArc(sketch, "E19.15.41.0", {"start": v(10.58, -23.43) * mm, "mid": v(10.76, -23.34) * mm, "end": v(10.94, -23.26) * mm});
            skArc(sketch, "E19.19.41.0", {"start": v(9.58, -22.15) * mm, "mid": v(10, -22.85) * mm, "end": v(10.58, -23.43) * mm});
            skLineSegment(sketch, "E19.23.41.0", {"start": v(9.33, -21.56) * mm, "end": v(9.58, -22.15) * mm});
            skArc(sketch, "E19.26.41.0", {"start": v(8.65, -21.85) * mm, "mid": v(9, -21.7) * mm, "end": v(9.33, -21.56) * mm});
            skArc(sketch, "E19.1.42.0", {"start": v(13.81, -19) * mm, "mid": v(13.5, -19.22) * mm, "end": v(13.2, -19.43) * mm});
            skLineSegment(sketch, "E19.4.42.0", {"start": v(13.2, -19.43) * mm, "end": v(13.56, -19.96) * mm});
            skArc(sketch, "E19.7.42.0", {"start": v(13.56, -19.96) * mm, "mid": v(13.93, -20.69) * mm, "end": v(14.11, -21.48) * mm});
            skArc(sketch, "E19.11.42.0", {"start": v(14.11, -21.48) * mm, "mid": v(13.94, -21.6) * mm, "end": v(13.77, -21.7) * mm});
            skArc(sketch, "E19.15.42.0", {"start": v(13.43, -21.92) * mm, "mid": v(13.6, -21.81) * mm, "end": v(13.77, -21.7) * mm});
            skArc(sketch, "E19.19.42.0", {"start": v(12.28, -20.77) * mm, "mid": v(12.78, -21.42) * mm, "end": v(13.43, -21.92) * mm});
            skLineSegment(sketch, "E19.23.42.0", {"start": v(11.96, -20.22) * mm, "end": v(12.28, -20.77) * mm});
            skArc(sketch, "E19.26.42.0", {"start": v(11.32, -20.59) * mm, "mid": v(11.64, -20.4) * mm, "end": v(11.96, -20.22) * mm});
            skArc(sketch, "E19.1.43.0", {"start": v(16.08, -17.13) * mm, "mid": v(15.81, -17.38) * mm, "end": v(15.54, -17.62) * mm});
            skLineSegment(sketch, "E19.4.43.0", {"start": v(15.54, -17.62) * mm, "end": v(15.96, -18.1) * mm});
            skArc(sketch, "E19.7.43.0", {"start": v(15.96, -18.1) * mm, "mid": v(16.42, -18.78) * mm, "end": v(16.7, -19.55) * mm});
            skArc(sketch, "E19.11.43.0", {"start": v(16.7, -19.55) * mm, "mid": v(16.54, -19.68) * mm, "end": v(16.38, -19.8) * mm});
            skArc(sketch, "E19.15.43.0", {"start": v(16.07, -20.06) * mm, "mid": v(16.23, -19.93) * mm, "end": v(16.38, -19.8) * mm});
            skArc(sketch, "E19.19.43.0", {"start": v(14.79, -19.07) * mm, "mid": v(15.37, -19.64) * mm, "end": v(16.07, -20.06) * mm});
            skLineSegment(sketch, "E19.23.43.0", {"start": v(14.4, -18.56) * mm, "end": v(14.79, -19.07) * mm});
            skArc(sketch, "E19.26.43.0", {"start": v(13.81, -19) * mm, "mid": v(14.1, -18.79) * mm, "end": v(14.4, -18.56) * mm});
            skArc(sketch, "E19.1.44.0", {"start": v(18.1, -14.98) * mm, "mid": v(17.87, -15.26) * mm, "end": v(17.62, -15.54) * mm});
            skLineSegment(sketch, "E19.4.44.0", {"start": v(17.62, -15.54) * mm, "end": v(18.1, -15.96) * mm});
            skArc(sketch, "E19.7.44.0", {"start": v(18.1, -15.96) * mm, "mid": v(18.64, -16.57) * mm, "end": v(19.01, -17.3) * mm});
            skArc(sketch, "E19.11.44.0", {"start": v(19.01, -17.3) * mm, "mid": v(18.88, -17.45) * mm, "end": v(18.74, -17.6) * mm});
            skArc(sketch, "E19.15.44.0", {"start": v(18.46, -17.89) * mm, "mid": v(18.6, -17.74) * mm, "end": v(18.74, -17.6) * mm});
            skArc(sketch, "E19.19.44.0", {"start": v(17.06, -17.06) * mm, "mid": v(17.7, -17.56) * mm, "end": v(18.46, -17.89) * mm});
            skLineSegment(sketch, "E19.23.44.0", {"start": v(16.61, -16.61) * mm, "end": v(17.06, -17.06) * mm});
            skArc(sketch, "E19.26.44.0", {"start": v(16.08, -17.13) * mm, "mid": v(16.35, -16.87) * mm, "end": v(16.61, -16.61) * mm});
            skArc(sketch, "E19.1.45.0", {"start": v(19.84, -12.59) * mm, "mid": v(19.64, -12.9) * mm, "end": v(19.43, -13.2) * mm});
            skLineSegment(sketch, "E19.4.45.0", {"start": v(19.43, -13.2) * mm, "end": v(19.96, -13.56) * mm});
            skArc(sketch, "E19.7.45.0", {"start": v(19.96, -13.56) * mm, "mid": v(20.57, -14.1) * mm, "end": v(21.03, -14.78) * mm});
            skArc(sketch, "E19.11.45.0", {"start": v(21.03, -14.78) * mm, "mid": v(20.91, -14.95) * mm, "end": v(20.8, -15.1) * mm});
            skArc(sketch, "E19.15.45.0", {"start": v(20.56, -15.43) * mm, "mid": v(20.68, -15.27) * mm, "end": v(20.8, -15.1) * mm});
            skArc(sketch, "E19.19.45.0", {"start": v(19.07, -14.79) * mm, "mid": v(19.77, -15.2) * mm, "end": v(20.56, -15.43) * mm});
            skLineSegment(sketch, "E19.23.45.0", {"start": v(18.56, -14.4) * mm, "end": v(19.07, -14.79) * mm});
            skArc(sketch, "E19.26.45.0", {"start": v(18.1, -14.98) * mm, "mid": v(18.34, -14.7) * mm, "end": v(18.56, -14.4) * mm});
            skArc(sketch, "E19.1.46.0", {"start": v(21.26, -10) * mm, "mid": v(21.1, -10.34) * mm, "end": v(20.93, -10.67) * mm});
            skLineSegment(sketch, "E19.4.46.0", {"start": v(20.93, -10.67) * mm, "end": v(21.5, -10.95) * mm});
            skArc(sketch, "E19.7.46.0", {"start": v(21.5, -10.95) * mm, "mid": v(22.18, -11.41) * mm, "end": v(22.72, -12.03) * mm});
            skArc(sketch, "E19.11.46.0", {"start": v(22.72, -12.03) * mm, "mid": v(22.62, -12.2) * mm, "end": v(22.53, -12.38) * mm});
            skArc(sketch, "E19.15.46.0", {"start": v(22.33, -12.74) * mm, "mid": v(22.43, -12.56) * mm, "end": v(22.53, -12.38) * mm});
            skArc(sketch, "E19.19.46.0", {"start": v(20.77, -12.28) * mm, "mid": v(21.52, -12.6) * mm, "end": v(22.33, -12.74) * mm});
            skLineSegment(sketch, "E19.23.46.0", {"start": v(20.22, -11.96) * mm, "end": v(20.77, -12.28) * mm});
            skArc(sketch, "E19.26.46.0", {"start": v(19.84, -12.59) * mm, "mid": v(20.03, -12.28) * mm, "end": v(20.22, -11.96) * mm});
            skArc(sketch, "E19.1.47.0", {"start": v(22.35, -7.26) * mm, "mid": v(22.23, -7.61) * mm, "end": v(22.1, -7.96) * mm});
            skLineSegment(sketch, "E19.4.47.0", {"start": v(22.1, -7.96) * mm, "end": v(22.7, -8.17) * mm});
            skArc(sketch, "E19.7.47.0", {"start": v(22.7, -8.17) * mm, "mid": v(23.43, -8.55) * mm, "end": v(24.05, -9.09) * mm});
            skArc(sketch, "E19.11.47.0", {"start": v(24.05, -9.09) * mm, "mid": v(23.97, -9.27) * mm, "end": v(23.9, -9.46) * mm});
            skArc(sketch, "E19.15.47.0", {"start": v(23.75, -9.84) * mm, "mid": v(23.82, -9.65) * mm, "end": v(23.9, -9.46) * mm});
            skArc(sketch, "E19.19.47.0", {"start": v(22.15, -9.58) * mm, "mid": v(22.93, -9.81) * mm, "end": v(23.75, -9.84) * mm});
            skLineSegment(sketch, "E19.23.47.0", {"start": v(21.56, -9.33) * mm, "end": v(22.15, -9.58) * mm});
            skArc(sketch, "E19.26.47.0", {"start": v(21.26, -10) * mm, "mid": v(21.41, -9.67) * mm, "end": v(21.56, -9.33) * mm});
            skArc(sketch, "E19.1.48.0", {"start": v(23.08, -4.4) * mm, "mid": v(23, -4.76) * mm, "end": v(22.93, -5.13) * mm});
            skLineSegment(sketch, "E19.4.48.0", {"start": v(22.93, -5.13) * mm, "end": v(23.55, -5.26) * mm});
            skArc(sketch, "E19.7.48.0", {"start": v(23.55, -5.26) * mm, "mid": v(24.32, -5.54) * mm, "end": v(25, -6) * mm});
            skArc(sketch, "E19.11.48.0", {"start": v(25, -6) * mm, "mid": v(24.95, -6.2) * mm, "end": v(24.9, -6.4) * mm});
            skArc(sketch, "E19.15.48.0", {"start": v(24.8, -6.78) * mm, "mid": v(24.85, -6.59) * mm, "end": v(24.9, -6.4) * mm});
            skArc(sketch, "E19.19.48.0", {"start": v(23.17, -6.73) * mm, "mid": v(23.98, -6.86) * mm, "end": v(24.8, -6.78) * mm});
            skLineSegment(sketch, "E19.23.48.0", {"start": v(22.56, -6.55) * mm, "end": v(23.17, -6.73) * mm});
            skArc(sketch, "E19.26.48.0", {"start": v(22.35, -7.26) * mm, "mid": v(22.46, -6.9) * mm, "end": v(22.56, -6.55) * mm});
            skArc(sketch, "E19.1.49.0", {"start": v(23.45, -1.48) * mm, "mid": v(23.42, -1.84) * mm, "end": v(23.4, -2.21) * mm});
            skLineSegment(sketch, "E19.4.49.0", {"start": v(23.4, -2.21) * mm, "end": v(24.02, -2.27) * mm});
            skArc(sketch, "E19.7.49.0", {"start": v(24.02, -2.27) * mm, "mid": v(24.82, -2.45) * mm, "end": v(25.55, -2.82) * mm});
            skArc(sketch, "E19.11.49.0", {"start": v(25.55, -2.82) * mm, "mid": v(25.53, -3.02) * mm, "end": v(25.5, -3.22) * mm});
            skArc(sketch, "E19.15.49.0", {"start": v(25.45, -3.62) * mm, "mid": v(25.48, -3.42) * mm, "end": v(25.5, -3.22) * mm});
            skArc(sketch, "E19.19.49.0", {"start": v(23.83, -3.77) * mm, "mid": v(24.65, -3.8) * mm, "end": v(25.45, -3.62) * mm});
            skLineSegment(sketch, "E19.23.49.0", {"start": v(23.2, -3.68) * mm, "end": v(23.83, -3.77) * mm});
            skArc(sketch, "E19.26.49.0", {"start": v(23.08, -4.4) * mm, "mid": v(23.15, -4.04) * mm, "end": v(23.2, -3.68) * mm});
            skSolve(sketch);
        }
        {
            var Q0;
            Q0 = qSketchRegion(id + "F0", true);
            extrude(context, id + "F1", {"entities" : qUnion([Q0]), "endBound" : BoundingType.SYMMETRIC, "depth" : 5.74 * mm});
        }
    });
